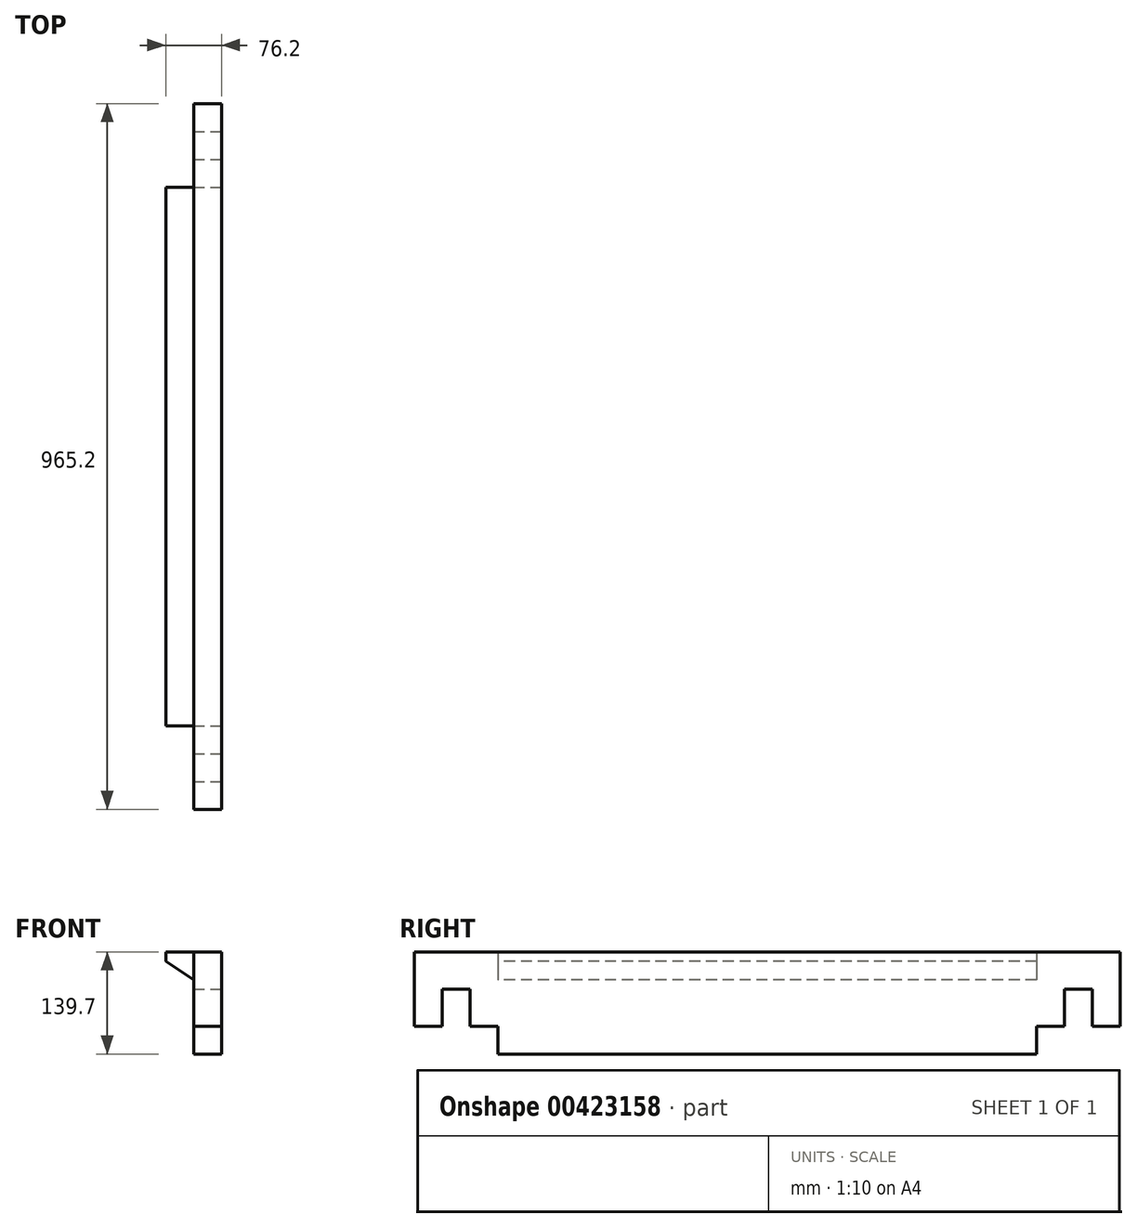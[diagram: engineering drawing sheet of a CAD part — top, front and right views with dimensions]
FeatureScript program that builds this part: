
annotation { "Feature Type Name" : "Feature", "Feature Type Description" : "" }
export const myFeature = defineFeature(function(context is Context, id is Id, definition is map)
    precondition{}
    {
        {
            var Q0;
            Q0=qCreatedBy(makeId("Top.planeOp"),FACE);
            var sketch = newSketch(context, id + "F0", { "sketchPlane" : qUnion([Q0])});
            skLineSegment(sketch, "E0.bottom", {"start": v(-19.05, 0) * mm, "end": v(19.05, 0) * mm});
            skLineSegment(sketch, "E0.top", {"start": v(-19.05, 482.6) * mm, "end": v(19.05, 482.6) * mm});
            skLineSegment(sketch, "E0.left", {"start": v(-19.05, 0) * mm, "end": v(-19.05, 482.6) * mm});
            skLineSegment(sketch, "E0.right", {"start": v(19.05, 0) * mm, "end": v(19.05, 482.6) * mm});
            skSolve(sketch);
        }
        {
            var Q0;
            Q0=makeQuery(id+"F0.imprint","IMPRINT",FACE,{"disambiguationData":[TD([[makeQuery(id+"F0.imprint","IMPRINT",EDGE,{"derivedFrom":sQuery(id+"F0.wireOp",EDGE,"E0.bottom")}),1.0]])]});
            extrude(context, id + "F1", {"entities" : qUnion([Q0]), "oppositeDirection" : true, "depth" : 139.7 * mm});
        }
        {
            var Q0;
            Q0=makeQuery(id+"F1.opExtrude","SWEPT_FACE",FACE,{"disambiguationData":[OSD([sQuery(id+"F0.wireOp",EDGE,"E0.right")])]});
            var sketch = newSketch(context, id + "F2", { "sketchPlane" : qUnion([Q0])});
            skLineSegment(sketch, "E1.bottom", {"start": v(0, -139.7) * mm, "end": v(114.3, -139.7) * mm});
            skLineSegment(sketch, "E1.top", {"start": v(0, -101.6) * mm, "end": v(114.3, -101.6) * mm});
            skLineSegment(sketch, "E1.left", {"start": v(0, -139.7) * mm, "end": v(0, -101.6) * mm});
            skLineSegment(sketch, "E1.right", {"start": v(114.3, -139.7) * mm, "end": v(114.3, -101.6) * mm});
            skSolve(sketch);
        }
        {
            var Q0;
            Q0=makeQuery(id+"F2.imprint","IMPRINT",FACE,{"disambiguationData":[TD([[makeQuery(id+"F2.imprint","IMPRINT",EDGE,{"derivedFrom":sQuery(id+"F2.wireOp",EDGE,"E1.bottom")}),1.0]])]});
            extrude(context, id + "F3", {"entities" : qUnion([Q0]), "operationType" : NewBodyOperationType.REMOVE, "endBound" : BoundingType.THROUGH_ALL, "oppositeDirection" : true, "depth" : 25.4 * mm});
        }
        {
            var Q0;
            Q0=makeQuery(id+"F1.opExtrude","SWEPT_FACE",FACE,{"disambiguationData":[OSD([sQuery(id+"F0.wireOp",EDGE,"E0.right")])]});
            var sketch = newSketch(context, id + "F4", { "sketchPlane" : qUnion([Q0])});
            skLineSegment(sketch, "E2.top", {"start": v(38.1, -50.8) * mm, "end": v(76.2, -50.8) * mm});
            skLineSegment(sketch, "E2.left", {"start": v(38.1, -50.8) * mm, "end": v(38.1, -101.6) * mm});
            skLineSegment(sketch, "E2.right", {"start": v(76.2, -50.8) * mm, "end": v(76.2, -101.6) * mm});
            skLineSegment(sketch, "E3", {"start": v(57.15, -50.8) * mm, "end": v(57.15, -101.6) * mm, "construction": true});
            skLineSegment(sketch, "E4", {"start": v(38.1, -50.8) * mm, "end": v(0, -50.8) * mm, "construction": true});
            skLineSegment(sketch, "E5", {"start": v(38.1, -101.6) * mm, "end": v(76.2, -101.6) * mm});
            skSolve(sketch);
        }
        {
            var Q0;
            Q0=makeQuery(id+"F4.imprint","IMPRINT",FACE,{"disambiguationData":[TD([[makeQuery(id+"F4.imprint","IMPRINT",EDGE,{"derivedFrom":sQuery(id+"F4.wireOp",EDGE,"E2.bottom")}),-1.0]])]});
            var Q1;
            Q1=makeQuery(id+"F4.imprint","IMPRINT",FACE,{"disambiguationData":[TD([[makeQuery(id+"F4.imprint","IMPRINT",EDGE,{"derivedFrom":sQuery(id+"F4.wireOp",EDGE,"E2.top")}),-1.0]])]});
            extrude(context, id + "F5", {"entities" : qUnion([Q0, Q1]), "operationType" : NewBodyOperationType.REMOVE, "endBound" : BoundingType.THROUGH_ALL, "oppositeDirection" : true, "depth" : 25.4 * mm});
        }
        {
            var Q0;
            Q0=makeQuery(id+"F1.opExtrude","SWEPT_FACE",FACE,{"disambiguationData":[OSD([sQuery(id+"F0.wireOp",EDGE,"E0.top")])]});
            cPlane(context, id + "F6", {"entities" : qUnion([Q0]), "cplaneType" : CPlaneType.OFFSET, "offset" : 0 * mm, "width" : 152.4 * mm, "height" : 152.4 * mm});
        }
        {
            var Q0;
            Q0=makeQuery(id+"F1.opExtrude","SWEPT_BODY",BODY,{"disambiguationData":[OSD([sQuery(id+"F0.wireOp",EDGE,"E0.bottom"),sQuery(id+"F0.wireOp",EDGE,"E0.top"),sQuery(id+"F0.wireOp",EDGE,"E0.left"),sQuery(id+"F0.wireOp",EDGE,"E0.right")])]});
            var Q1;
            Q1=qCreatedBy(id+"F6.planeOp",FACE);
            mirror(context, id + "F7", {"operationType" : NewBodyOperationType.ADD, "entities" : qUnion([Q0]), "mirrorPlane" : qUnion([Q1])});
        }
        {
            var Q0;
            Q0=qCreatedBy(id+"F6.planeOp",FACE);
            var sketch = newSketch(context, id + "F8", { "sketchPlane" : qUnion([Q0])});
            skLineSegment(sketch, "E6", {"start": v(57.15, 0) * mm, "end": v(19.05, 0) * mm});
            skLineSegment(sketch, "E7", {"start": v(19.05, 0) * mm, "end": v(19.05, -38.1) * mm});
            skLineSegment(sketch, "E8", {"start": v(57.15, 0) * mm, "end": v(57.15, -12.7) * mm});
            skLineSegment(sketch, "E9", {"start": v(57.15, -12.7) * mm, "end": v(19.05, -38.1) * mm});
            skSolve(sketch);
        }
        {
            var Q0;
            Q0=makeQuery(id+"F8.imprint","IMPRINT",FACE,{"disambiguationData":[TD([[makeQuery(id+"F8.imprint","IMPRINT",EDGE,{"derivedFrom":sQuery(id+"F8.wireOp",EDGE,"E6")}),1.0]])]});
            extrude(context, id + "F9", {"entities" : qUnion([Q0]), "depth" : 368.3 * mm, "hasSecondDirection" : true, "secondDirectionOppositeDirection" : true, "secondDirectionDepth" : 368.3 * mm});
        }
    });
